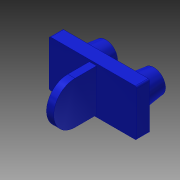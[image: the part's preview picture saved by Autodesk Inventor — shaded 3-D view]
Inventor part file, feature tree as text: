
AUTODESK INVENTOR PART (.ipt)
format: ipt  version: 2015 (Build 190159000, 159)  size: 128,000 bytes
history: native  units: mm
features: sketch x3, extrude x2, fillet x1, revolve x1, mirror x1
ambient origin geometry x8: Origin, YZ Plane, XZ Plane, XY Plane, X Axis, Y Axis, Z Axis, Center Point
bodies: Solid1 (feature_tree)
feature tree (8):
  extrude  "Extrusion1"  Depth=7.75mm
  fillet  "Fillet1"  Radius=2.15mm
  extrude  "Extrusion2"  Depth=0.25mm
  revolve  "Revolution1"  [1 undecoded]
  mirror  "Mirror1"
  sketch  "Sketch1"  dims[d0=14.6mm d1=7.75mm d2=2.15mm d3=0.0mm]
  sketch  "Sketch2"  dims[d4=0.25mm d5=3.6mm]
  sketch  "Sketch3"  dims[d6=7.08mm d7=1.2mm d8=0.0mm d9=4.88mm d10=3.88mm d11=4.0mm d12=4.0mm d13=90.0deg]
note: 1 required parameter value undecoded (feature->parameter linkage not recoverable at this tier; creation-order binding heuristic only, values carry confidence <= 0.55)
